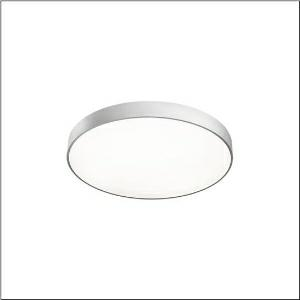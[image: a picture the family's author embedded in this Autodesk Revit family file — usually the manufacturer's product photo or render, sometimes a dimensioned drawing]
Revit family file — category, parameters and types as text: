
# Revit family: round_21_m_51mr36gm8421s
name_source: partatom
category: Lighting Fixtures
units: mm (PartAtom-declared; Revit-internal decimal feet)

## family parameters
Cut with Voids When Loaded = No
Host = Face
Light Source = No
Part Type = Normal
Room Calculation Point = No
Round Connector Dimension = Use Diameter
Shared = No

## types (1)
- --- (1 x LED, 8960 lm, 62.3 W, 4000K)
    Apparent Load = 62 VA
    CIE Flux Codes = 49 80 96 85 100
    Color Rendering = 80
    Color Temperature = 4000K
    Default Elevation = 1800 mm
    Description = Round 21 M, wall and ceiling luminaire, primary optical cover: cover, of PMMA, opal, light emission: direct/indirect distribution, primary light characteristic: symmetric, installation type: suspended mounting, surface-mounted, LED, rated luminous flux: 8.190lm, luminous efficacy: 135lm/W, light colour: 840, colour temperature: 4000K, control gear: ON/OFF Multilumen, with terminal, 3-pole, mains connection: 230V, AC, 50/60Hz, rated input power: 61W, housing, of aluminium, coated, silver, diameter: 600mm, height: 62mm, protection rating (complete): IP40, insulation class (complete): insulation class I (protective earthing), certification: CE, impact resistance: IK04, permissible operating ambient temperature: -10..+35°C, packaging unit: 1 piece
    Height = 87 mm
    Lamp = 1 x LED
    Lamp Light Flux = 8960 lm
    Lamp Power = 62.3 W
    Lamp count = 1
    Length = 600 mm
    Luminous efficacy = 144 lm/W
    Manufacturer = Siteco
    ModVariant = No
    Model = 51MR36GM8421S
    Mounting Place = Ceiling
    Mounting Type = Surface mounted
    Number of Poles = 1
    OnlyDefault = Yes
    Power Factor = 1
    Product Name = Round 21 M
    Product group = wall and ceiling luminaire
    ProductGroupID = 304
    Protection Class = Protection class I
    Protection Degree = IP 40
    RLX_Detail_Level = 1
    RLX_Emergency_Light_Flux = 0 lm
    RLX_Emergency_Type = 0
    RLX_Emergency_Type_DB = No
    RlxData = <blob elided: 17933 chars, md5=374be869>
    Socket = socket
    Standby Power = 0 W
    System Light Flux = 8960 lm
    System Power = 62 W
    Type Comments = factory setting: luminous flux: 100 % | (ON | ON | ON | ON) | 700 mA
    Type Image = l_1258303.jpg
    URL = http://relux.com
    VarID = @adj_032654
    Voltage = 0 V
    Weight = 0.00 kg
    Width = 0 mm  [stored 0 ft]

note: [stored X ft] marks values corroborated as IEEE doubles in the binary element streams (Revit-internal decimal feet)

## geometry (parser evidence)
native form markers: Blend x4, Sweep x12
no freeform markers — native parametric forms only
